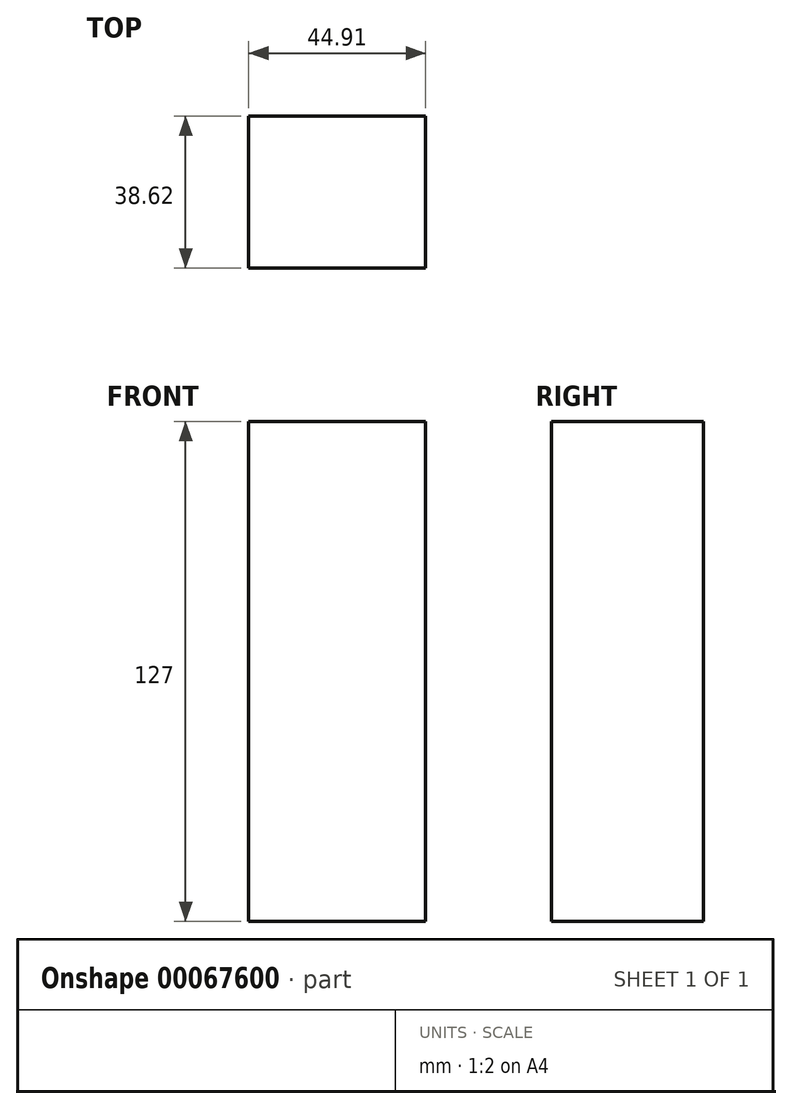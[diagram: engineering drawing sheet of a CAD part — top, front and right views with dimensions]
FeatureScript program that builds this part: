
annotation { "Feature Type Name" : "Feature", "Feature Type Description" : "" }
export const myFeature = defineFeature(function(context is Context, id is Id, definition is map)
    precondition{}
    {
        {
            var Q0;
            Q0=qCreatedBy(makeId("Top.planeOp"),FACE);
            var sketch = newSketch(context, id + "F0", { "sketchPlane" : qUnion([Q0])});
            skLineSegment(sketch, "E0.rect.bottom", {"start": v(-9.04, 10.6) * mm, "end": v(-53.95, 10.6) * mm});
            skLineSegment(sketch, "E0.rect.top", {"start": v(-9.04, 49.21) * mm, "end": v(-53.95, 49.21) * mm});
            skLineSegment(sketch, "E0.rect.left", {"start": v(-9.04, 10.6) * mm, "end": v(-9.04, 49.21) * mm});
            skLineSegment(sketch, "E0.rect.right", {"start": v(-53.95, 10.6) * mm, "end": v(-53.95, 49.21) * mm});
            skPoint(sketch, "E0.rect.middle", {"position": v(-31.5, 29.9) * mm});
            skSolve(sketch);
        }
        {
            var Q0;
            Q0=makeQuery(id+"F0.imprint","IMPRINT",FACE,{"disambiguationData":[TD([[makeQuery(id+"F0.imprint","IMPRINT",EDGE,{"derivedFrom":sQuery(id+"F0.wireOp",EDGE,"E0.rect.bottom")}),-1.0]])]});
            extrude(context, id + "F1", {"entities" : qUnion([Q0]), "depth" : 127 * mm});
        }
    });
